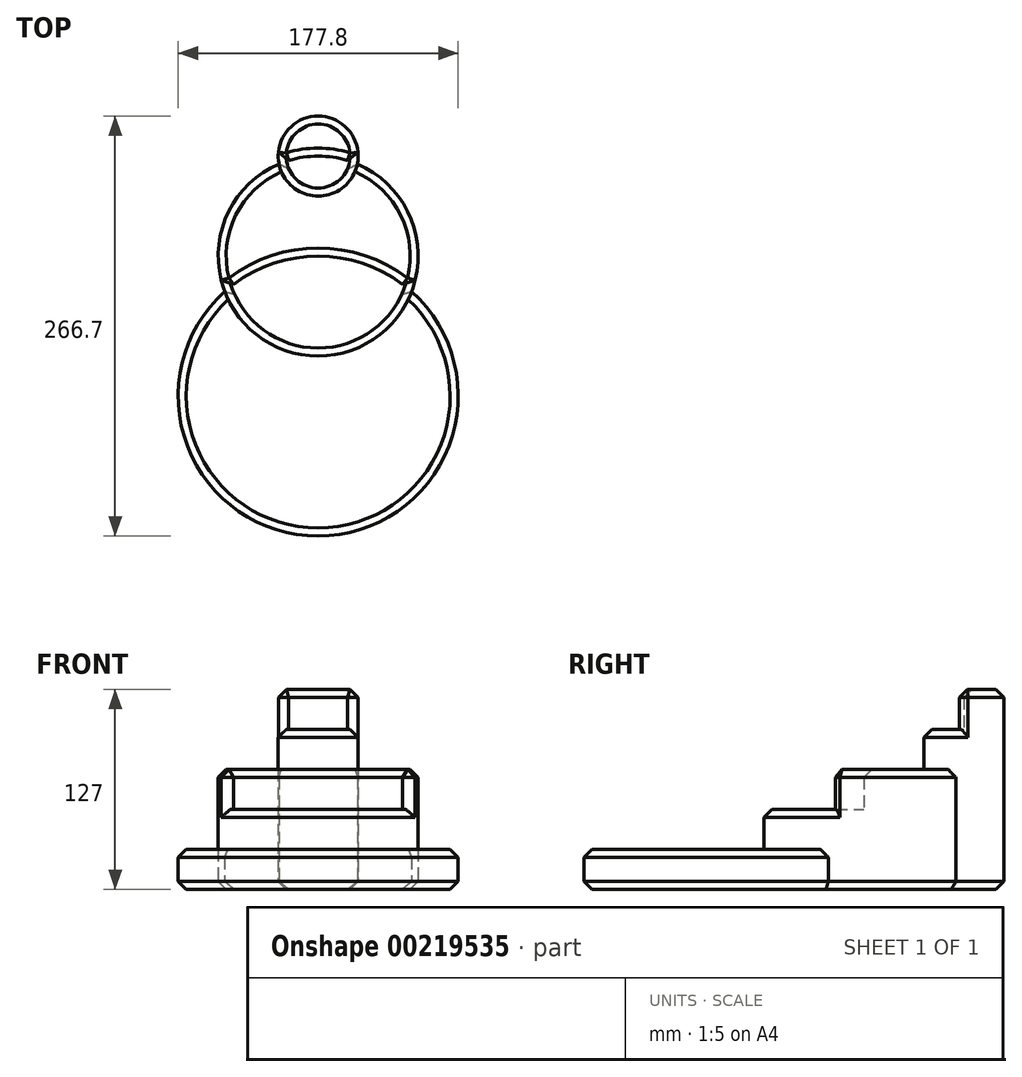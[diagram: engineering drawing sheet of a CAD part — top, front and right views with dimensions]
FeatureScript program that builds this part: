
annotation { "Feature Type Name" : "Feature", "Feature Type Description" : "" }
export const myFeature = defineFeature(function(context is Context, id is Id, definition is map)
    precondition{}
    {
        {
            var Q0;
            Q0=qCreatedBy(makeId("Top.planeOp"),FACE);
            var sketch = newSketch(context, id + "F0", { "sketchPlane" : qUnion([Q0])});
            skCircle(sketch, "E0", {"center": v(0, 0) * mm, "radius": 88.9 * mm});
            skCircle(sketch, "E1", {"center": v(0, 88.9) * mm, "radius": 63.5 * mm});
            skCircle(sketch, "E2", {"center": v(0, 152.4) * mm, "radius": 25.4 * mm});
            skLineSegment(sketch, "E3", {"start": v(0, 0) * mm, "end": v(0, 152.4) * mm, "construction": true});
            skSolve(sketch);
        }
        {
            var Q0;
            {var subQ0=sQuery(id+"F0.wireOp",EDGE,"E1");var subQ1=sQuery(id+"F0.wireOp",EDGE,"E0");var subQ2=makeQuery(id+"F0.imprint","INTERSECT",VERTEX,{"disambiguationData":[OD(0.0)],"derivedFrom":[subQ1,subQ0]});Q0=makeQuery(id+"F0.imprint","IMPRINT",FACE,{"disambiguationData":[TD([[makeQuery(id+"F0.imprint","IMPRINT",EDGE,{"disambiguationData":[TD([[subQ2,-1.0]])],"derivedFrom":subQ1}),1.0]])]});}
            extrude(context, id + "F1", {"entities" : qUnion([Q0]), "depth" : 25.4 * mm});
        }
        {
            var Q0;
            {var subQ0=sQuery(id+"F0.wireOp",EDGE,"E1");var subQ1=sQuery(id+"F0.wireOp",EDGE,"E0");var subQ2=makeQuery(id+"F0.imprint","INTERSECT",VERTEX,{"disambiguationData":[OD(0.0)],"derivedFrom":[subQ1,subQ0]});Q0=makeQuery(id+"F0.imprint","IMPRINT",FACE,{"disambiguationData":[TD([[makeQuery(id+"F0.imprint","IMPRINT",EDGE,{"disambiguationData":[TD([[subQ2,1.0]])],"derivedFrom":subQ1}),1.0]])]});}
            extrude(context, id + "F2", {"entities" : qUnion([Q0]), "operationType" : NewBodyOperationType.ADD, "depth" : 50.8 * mm});
        }
        {
            var Q0;
            {var subQ0=sQuery(id+"F0.wireOp",EDGE,"E1");var subQ1=sQuery(id+"F0.wireOp",EDGE,"E0");var subQ2=makeQuery(id+"F0.imprint","INTERSECT",VERTEX,{"disambiguationData":[OD(0.0)],"derivedFrom":[subQ1,subQ0]});Q0=makeQuery(id+"F0.imprint","IMPRINT",FACE,{"disambiguationData":[TD([[makeQuery(id+"F0.imprint","IMPRINT",EDGE,{"disambiguationData":[TD([[subQ2,1.0]])],"derivedFrom":subQ1}),-1.0]])]});}
            extrude(context, id + "F3", {"entities" : qUnion([Q0]), "operationType" : NewBodyOperationType.ADD, "depth" : 76.2 * mm});
        }
        {
            var Q0;
            {var subQ0=sQuery(id+"F0.wireOp",EDGE,"E2");var subQ1=sQuery(id+"F0.wireOp",EDGE,"E1");var subQ2=makeQuery(id+"F0.imprint","INTERSECT",VERTEX,{"disambiguationData":[OD(0.0)],"derivedFrom":[subQ1,subQ0]});Q0=makeQuery(id+"F0.imprint","IMPRINT",FACE,{"disambiguationData":[TD([[makeQuery(id+"F0.imprint","IMPRINT",EDGE,{"disambiguationData":[TD([[subQ2,1.0]])],"derivedFrom":subQ1}),1.0]])]});}
            extrude(context, id + "F4", {"entities" : qUnion([Q0]), "operationType" : NewBodyOperationType.ADD, "depth" : 101.6 * mm});
        }
        {
            var Q0;
            {var subQ0=sQuery(id+"F0.wireOp",EDGE,"E2");var subQ1=sQuery(id+"F0.wireOp",EDGE,"E1");var subQ2=makeQuery(id+"F0.imprint","INTERSECT",VERTEX,{"disambiguationData":[OD(0.0)],"derivedFrom":[subQ1,subQ0]});Q0=makeQuery(id+"F0.imprint","IMPRINT",FACE,{"disambiguationData":[TD([[makeQuery(id+"F0.imprint","IMPRINT",EDGE,{"disambiguationData":[TD([[subQ2,1.0]])],"derivedFrom":subQ1}),-1.0]])]});}
            extrude(context, id + "F5", {"entities" : qUnion([Q0]), "operationType" : NewBodyOperationType.ADD, "depth" : 127 * mm});
        }
        {
            var Q0;
            Q0=makeQuery(id+"F5.opExtrude","CAP_EDGE",EDGE,{"disambiguationData":[OSD([sQuery(id+"F0.wireOp",EDGE,"E1")])],"isStart":false});
            var Q1;
            Q1=makeQuery(id+"F4.opExtrude","CAP_EDGE",EDGE,{"disambiguationData":[OSD([sQuery(id+"F0.wireOp",EDGE,"E2")])],"isStart":false});
            var Q2;
            Q2=makeQuery(id+"F3.opExtrude","CAP_EDGE",EDGE,{"disambiguationData":[OSD([sQuery(id+"F0.wireOp",EDGE,"E2")])],"isStart":false});
            var Q3;
            Q3=makeQuery(id+"F3.opExtrude","CAP_EDGE",EDGE,{"disambiguationData":[OSD([sQuery(id+"F0.wireOp",EDGE,"E0")])],"isStart":false});
            var Q4;
            Q4=makeQuery(id+"F2.opExtrude","CAP_EDGE",EDGE,{"disambiguationData":[OSD([sQuery(id+"F0.wireOp",EDGE,"E0")])],"isStart":false});
            var Q5;
            Q5=makeQuery(id+"F2.opExtrude","CAP_EDGE",EDGE,{"disambiguationData":[OSD([sQuery(id+"F0.wireOp",EDGE,"E1")])],"isStart":false});
            var Q6;
            Q6=makeQuery(id+"F1.opExtrude","CAP_EDGE",EDGE,{"disambiguationData":[OSD([sQuery(id+"F0.wireOp",EDGE,"E1")])],"isStart":false});
            var Q7;
            Q7=makeQuery(id+"F1.opExtrude","CAP_EDGE",EDGE,{"disambiguationData":[OSD([sQuery(id+"F0.wireOp",EDGE,"E0")])],"isStart":false});
            var Q8;
            {var subQ0=sQuery(id+"F0.wireOp",EDGE,"E1");var subQ1=sQuery(id+"F0.wireOp",EDGE,"E2");Q8=makeQuery(id+"F5.boolean.opBoolean","SPLIT",EDGE,{"disambiguationData":[TD([makeQuery(id+"F5.opExtrude","SWEPT_FACE",FACE,{"disambiguationData":[OSD([subQ0])]})])],"derivedFrom":makeQuery(id+"F5.opExtrude","SWEPT_EDGE",EDGE,{"disambiguationData":[OSD([subQ0,subQ1]),TDD([makeQuery(id+"F0.imprint","INTERSECT",VERTEX,{"disambiguationData":[OD(0.0)],"derivedFrom":[subQ0,subQ1]})])]})});}
            var Q9;
            {var subQ0=sQuery(id+"F0.wireOp",EDGE,"E1");var subQ1=sQuery(id+"F0.wireOp",EDGE,"E2");Q9=makeQuery(id+"F5.boolean.opBoolean","SPLIT",EDGE,{"disambiguationData":[TD([makeQuery(id+"F5.opExtrude","SWEPT_FACE",FACE,{"disambiguationData":[OSD([subQ0])]})])],"derivedFrom":makeQuery(id+"F5.opExtrude","SWEPT_EDGE",EDGE,{"disambiguationData":[OSD([subQ0,subQ1]),TDD([makeQuery(id+"F0.imprint","INTERSECT",VERTEX,{"disambiguationData":[OD(1.0)],"derivedFrom":[subQ0,subQ1]})])]})});}
            var Q10;
            {var subQ0=sQuery(id+"F0.wireOp",EDGE,"E1");Q10=makeQuery(id+"F3.opExtrude","CAP_EDGE",EDGE,{"disambiguationData":[OSD([subQ0]),TDD([makeQuery(id+"F0.imprint","IMPRINT",EDGE,{"disambiguationData":[TD([[makeQuery(id+"F0.imprint","INTERSECT",VERTEX,{"disambiguationData":[OD(0.0)],"derivedFrom":[sQuery(id+"F0.wireOp",EDGE,"E0"),subQ0]}),1.0]])],"derivedFrom":subQ0})])],"isStart":false});}
            var Q11;
            {var subQ0=sQuery(id+"F0.wireOp",EDGE,"E1");Q11=makeQuery(id+"F3.opExtrude","CAP_EDGE",EDGE,{"disambiguationData":[OSD([subQ0]),TDD([makeQuery(id+"F0.imprint","IMPRINT",EDGE,{"disambiguationData":[TD([[makeQuery(id+"F0.imprint","INTERSECT",VERTEX,{"disambiguationData":[OD(1.0)],"derivedFrom":[sQuery(id+"F0.wireOp",EDGE,"E0"),subQ0]}),-1.0]])],"derivedFrom":subQ0})])],"isStart":false});}
            var Q12;
            Q12=makeQuery(id+"F5.opExtrude","CAP_EDGE",EDGE,{"disambiguationData":[OSD([sQuery(id+"F0.wireOp",EDGE,"E2")])],"isStart":false});
            var Q13;
            {var subQ0=sQuery(id+"F0.wireOp",EDGE,"E0");var subQ1=sQuery(id+"F0.wireOp",EDGE,"E1");var subQ3=makeQuery(id+"F0.imprint","INTERSECT",VERTEX,{"disambiguationData":[OD(0.0)],"derivedFrom":[subQ0,subQ1]});Q13=makeQuery(id+"F3.boolean.opBoolean","SPLIT",EDGE,{"disambiguationData":[TD([makeQuery(id+"F1.opExtrude","SWEPT_FACE",FACE,{"disambiguationData":[OSD([subQ0])]})])],"derivedFrom":makeQuery(id+"F3.opExtrude","SWEPT_EDGE",EDGE,{"disambiguationData":[OSD([subQ0,subQ1]),TDD([subQ3])]})});}
            var Q14;
            {var subQ1=sQuery(id+"F0.wireOp",EDGE,"E1");var subQ2=sQuery(id+"F0.wireOp",EDGE,"E0");var subQ3=makeQuery(id+"F0.imprint","INTERSECT",VERTEX,{"disambiguationData":[OD(0.0)],"derivedFrom":[subQ2,subQ1]});Q14=makeQuery(id+"F3.boolean.opBoolean","SPLIT",EDGE,{"disambiguationData":[TD([makeQuery(id+"F3.opExtrude","SWEPT_FACE",FACE,{"disambiguationData":[OSD([subQ2])]})])],"derivedFrom":makeQuery(id+"F3.opExtrude","SWEPT_EDGE",EDGE,{"disambiguationData":[OSD([subQ2,subQ1]),TDD([subQ3])]})});}
            var Q15;
            {var subQ0=sQuery(id+"F0.wireOp",EDGE,"E0");var subQ1=sQuery(id+"F0.wireOp",EDGE,"E1");var subQ3=makeQuery(id+"F0.imprint","INTERSECT",VERTEX,{"disambiguationData":[OD(1.0)],"derivedFrom":[subQ0,subQ1]});Q15=makeQuery(id+"F3.boolean.opBoolean","SPLIT",EDGE,{"disambiguationData":[TD([makeQuery(id+"F1.opExtrude","SWEPT_FACE",FACE,{"disambiguationData":[OSD([subQ0])]})])],"derivedFrom":makeQuery(id+"F3.opExtrude","SWEPT_EDGE",EDGE,{"disambiguationData":[OSD([subQ0,subQ1]),TDD([subQ3])]})});}
            var Q16;
            {var subQ1=sQuery(id+"F0.wireOp",EDGE,"E1");var subQ2=sQuery(id+"F0.wireOp",EDGE,"E0");var subQ3=makeQuery(id+"F0.imprint","INTERSECT",VERTEX,{"disambiguationData":[OD(1.0)],"derivedFrom":[subQ2,subQ1]});Q16=makeQuery(id+"F3.boolean.opBoolean","SPLIT",EDGE,{"disambiguationData":[TD([makeQuery(id+"F3.opExtrude","SWEPT_FACE",FACE,{"disambiguationData":[OSD([subQ2])]})])],"derivedFrom":makeQuery(id+"F3.opExtrude","SWEPT_EDGE",EDGE,{"disambiguationData":[OSD([subQ2,subQ1]),TDD([subQ3])]})});}
            var Q17;
            {var subQ0=sQuery(id+"F0.wireOp",EDGE,"E2");var subQ1=sQuery(id+"F0.wireOp",EDGE,"E1");var subQ3=makeQuery(id+"F0.imprint","INTERSECT",VERTEX,{"disambiguationData":[OD(1.0)],"derivedFrom":[subQ1,subQ0]});Q17=makeQuery(id+"F5.boolean.opBoolean","SPLIT",EDGE,{"disambiguationData":[TD([makeQuery(id+"F2.opExtrude","SWEPT_FACE",FACE,{"disambiguationData":[OSD([subQ1])]})])],"derivedFrom":makeQuery(id+"F5.opExtrude","SWEPT_EDGE",EDGE,{"disambiguationData":[OSD([subQ1,subQ0]),TDD([subQ3])]})});}
            var Q18;
            {var subQ0=sQuery(id+"F0.wireOp",EDGE,"E2");var subQ1=sQuery(id+"F0.wireOp",EDGE,"E1");var subQ3=makeQuery(id+"F0.imprint","INTERSECT",VERTEX,{"disambiguationData":[OD(0.0)],"derivedFrom":[subQ1,subQ0]});Q18=makeQuery(id+"F5.boolean.opBoolean","SPLIT",EDGE,{"disambiguationData":[TD([makeQuery(id+"F2.opExtrude","SWEPT_FACE",FACE,{"disambiguationData":[OSD([subQ1])]})])],"derivedFrom":makeQuery(id+"F5.opExtrude","SWEPT_EDGE",EDGE,{"disambiguationData":[OSD([subQ1,subQ0]),TDD([subQ3])]})});}
            var Q19;
            {var subQ0=sQuery(id+"F0.wireOp",EDGE,"E0");Q19=makeQuery(id+"F2.boolean.opBoolean","MERGE",EDGE,{"derivedFrom":[makeQuery(id+"F1.opExtrude","CAP_EDGE",EDGE,{"disambiguationData":[OSD([subQ0])],"isStart":true}),makeQuery(id+"F2.opExtrude","CAP_EDGE",EDGE,{"disambiguationData":[OSD([subQ0])],"isStart":true})]});}
            var Q20;
            {var subQ0=sQuery(id+"F0.wireOp",EDGE,"E1");var subQ1=sQuery(id+"F0.wireOp",EDGE,"E0");Q20=makeQuery(id+"F5.boolean.opBoolean","SPLIT",EDGE,{"disambiguationData":[OD(0.0)],"derivedFrom":makeQuery(id+"F4.boolean.opBoolean","MERGE",EDGE,{"derivedFrom":[makeQuery(id+"F3.opExtrude","CAP_EDGE",EDGE,{"disambiguationData":[OSD([subQ0]),TDD([makeQuery(id+"F0.imprint","IMPRINT",EDGE,{"disambiguationData":[TD([[makeQuery(id+"F0.imprint","INTERSECT",VERTEX,{"disambiguationData":[OD(0.0)],"derivedFrom":[subQ1,subQ0]}),1.0]])],"derivedFrom":subQ0})])],"isStart":true}),makeQuery(id+"F3.opExtrude","CAP_EDGE",EDGE,{"disambiguationData":[OSD([subQ0]),TDD([makeQuery(id+"F0.imprint","IMPRINT",EDGE,{"disambiguationData":[TD([[makeQuery(id+"F0.imprint","INTERSECT",VERTEX,{"disambiguationData":[OD(1.0)],"derivedFrom":[subQ1,subQ0]}),-1.0]])],"derivedFrom":subQ0})])],"isStart":true}),makeQuery(id+"F4.opExtrude","CAP_EDGE",EDGE,{"disambiguationData":[OSD([subQ0])],"isStart":true})]})});}
            var Q21;
            Q21=makeQuery(id+"F5.opExtrude","CAP_EDGE",EDGE,{"disambiguationData":[OSD([sQuery(id+"F0.wireOp",EDGE,"E2")])],"isStart":true});
            var Q22;
            {var subQ0=sQuery(id+"F0.wireOp",EDGE,"E1");var subQ1=sQuery(id+"F0.wireOp",EDGE,"E0");Q22=makeQuery(id+"F5.boolean.opBoolean","SPLIT",EDGE,{"disambiguationData":[OD(1.0)],"derivedFrom":makeQuery(id+"F4.boolean.opBoolean","MERGE",EDGE,{"derivedFrom":[makeQuery(id+"F3.opExtrude","CAP_EDGE",EDGE,{"disambiguationData":[OSD([subQ0]),TDD([makeQuery(id+"F0.imprint","IMPRINT",EDGE,{"disambiguationData":[TD([[makeQuery(id+"F0.imprint","INTERSECT",VERTEX,{"disambiguationData":[OD(0.0)],"derivedFrom":[subQ1,subQ0]}),1.0]])],"derivedFrom":subQ0})])],"isStart":true}),makeQuery(id+"F3.opExtrude","CAP_EDGE",EDGE,{"disambiguationData":[OSD([subQ0]),TDD([makeQuery(id+"F0.imprint","IMPRINT",EDGE,{"disambiguationData":[TD([[makeQuery(id+"F0.imprint","INTERSECT",VERTEX,{"disambiguationData":[OD(1.0)],"derivedFrom":[subQ1,subQ0]}),-1.0]])],"derivedFrom":subQ0})])],"isStart":true}),makeQuery(id+"F4.opExtrude","CAP_EDGE",EDGE,{"disambiguationData":[OSD([subQ0])],"isStart":true})]})});}
            chamfer(context, id + "F6", {"entities" : qUnion([Q0, Q1, Q2, Q3, Q4, Q5, Q6, Q7, Q8, Q9, Q10, Q11, Q12, Q13, Q14, Q15, Q16, Q17, Q18, Q19, Q20, Q21, Q22]), "width" : 5.08 * mm, "tangentPropagation" : true});
        }
    });
